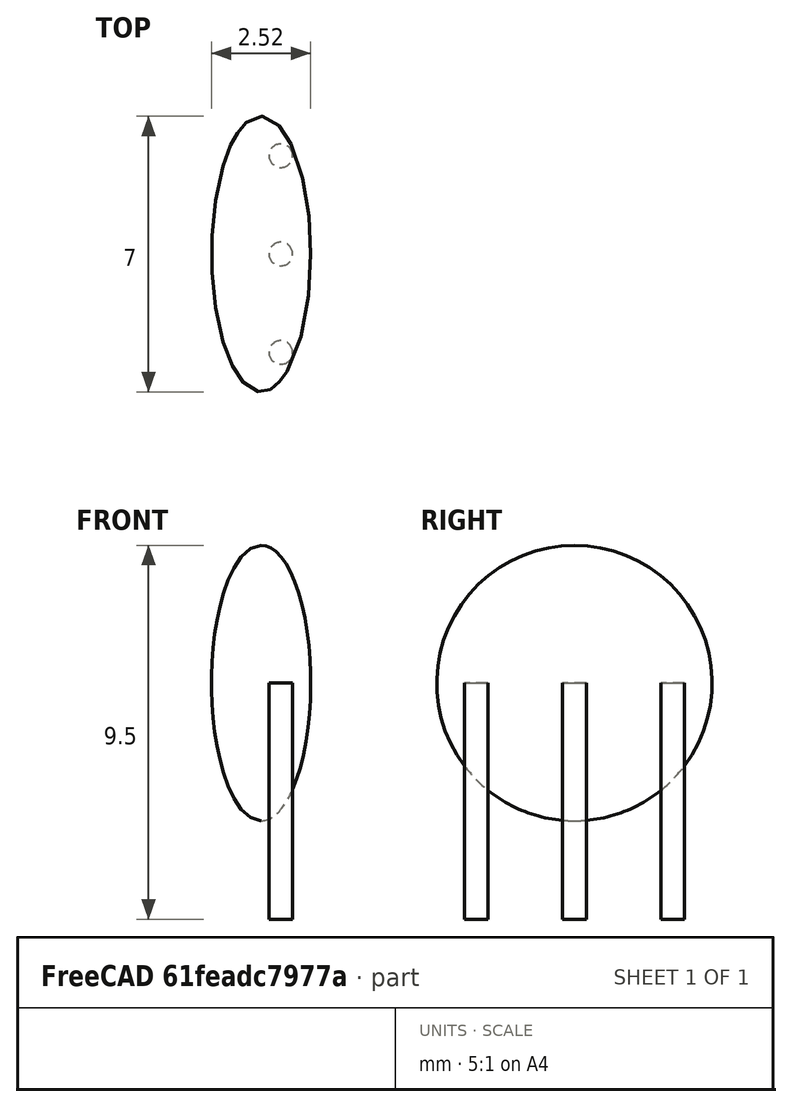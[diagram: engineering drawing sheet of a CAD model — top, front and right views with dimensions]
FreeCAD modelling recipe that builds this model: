
FCSTD DOCUMENT  (FreeCAD 0.18R4 (GitTag))
Label: DSN6
License: All rights reserved
LicenseURL: http://en.wikipedia.org/wiki/All_rights_reserved
objects: Part::Cylinder×3, PartDesign::Body×2, Part::Sphere×1, Part::FeaturePython×1, Part::Compound×1
note: 8 computed .brp shape members not serialized (recipe doc carries the construction recipe); baked Part::Feature solids carry a one-line shape summary decoded from their .brp

FEATURE [PartDesign::Body] Body
  Origin = -> Origin
FEATURE [Part::Sphere] Sphere
  Angle1 = -90
  Angle2 = 90
  Angle3 = 360
  AttacherType = Attacher::AttachEngine3D
  Placement = pos=(0,0,-1) rot=(0,0,1;0rad)
  Radius = 3.5
FEATURE [Part::FeaturePython] Scale  # Draft clone (typed FeaturePython)
  Fuse = false
  Objects = -> [Sphere]
  Scale = (0.36,1,1)
FEATURE [PartDesign::Body] Body001  label="Legs"
  Origin = -> Origin001
FEATURE [Part::Cylinder] Cylinder
  Angle = 360
  AttacherType = Attacher::AttachEngine3D
  Height = 6
  Placement = pos=(0.5,0,-6) rot=(0,0,1;0rad)
  Radius = 0.3
FEATURE [Part::Cylinder] Cylinder001
  Angle = 360
  AttacherType = Attacher::AttachEngine3D
  Height = 6
  Placement = pos=(0.5,2.5,-6) rot=(0,0,1;0rad)
  Radius = 0.3
FEATURE [Part::Cylinder] Cylinder002
  Angle = 360
  AttacherType = Attacher::AttachEngine3D
  Height = 6
  Placement = pos=(0.5,-2.5,-6) rot=(0,0,1;0rad)
  Radius = 0.3
FEATURE [Part::Compound] Compound
  Links = -> [Body001,Body]
